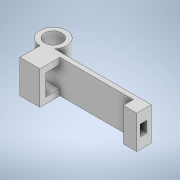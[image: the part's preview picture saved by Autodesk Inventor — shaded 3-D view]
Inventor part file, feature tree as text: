
AUTODESK INVENTOR PART (.ipt)
format: ipt  version: 2020 (Build 240168000, 168)  size: 158,720 bytes
history: native  units: in
note: dims shown in document units (in); Inventor stores cm internally (conversion verified against a paired STEP export)
features: extrude x6, sketch x6, plane x1
ambient origin geometry x8: Origin, YZ Plane, XZ Plane, XY Plane, X Axis, Y Axis, Z Axis, Center Point
bodies: Solid1 (feature_tree)
feature tree (13):
  extrude  "Extrusion1"  Depth=0.315in
  plane  "Work Plane1"
  extrude  "Extrusion2"  Depth=0.1575in
  extrude  "Extrusion3"  Depth=1.2598in
  extrude  "Extrusion4"  Depth=0.2362in
  extrude  "Extrusion5"  Depth=0.2362in
  extrude  "Extrusion6"  Depth=0.1673in
  sketch  "Sketch1"  dims[d0=0.2067in d1=0.315in]
  sketch  "Sketch2"  dims[d2=0.3937in d3=0.0in d4=0.1575in]
  sketch  "Sketch3"  dims[d5=1.2598in d6=1.2598in]
  sketch  "Sketch4"  dims[d7=0.0541in d8=0.0in d9=0.2362in]
  sketch  "Sketch5"  dims[d10=0.2362in d11=0.0in d12=0.123in]
  sketch  "Sketch6"  dims[d13=0.123in d14=0.1673in d15=0.2362in d16=0.0in d17=0.1575in d18=0.1181in d19=0.0in d20=0.064in d21=0.064in d22=0.0787in d23=0.1181in d24=0.0in]
